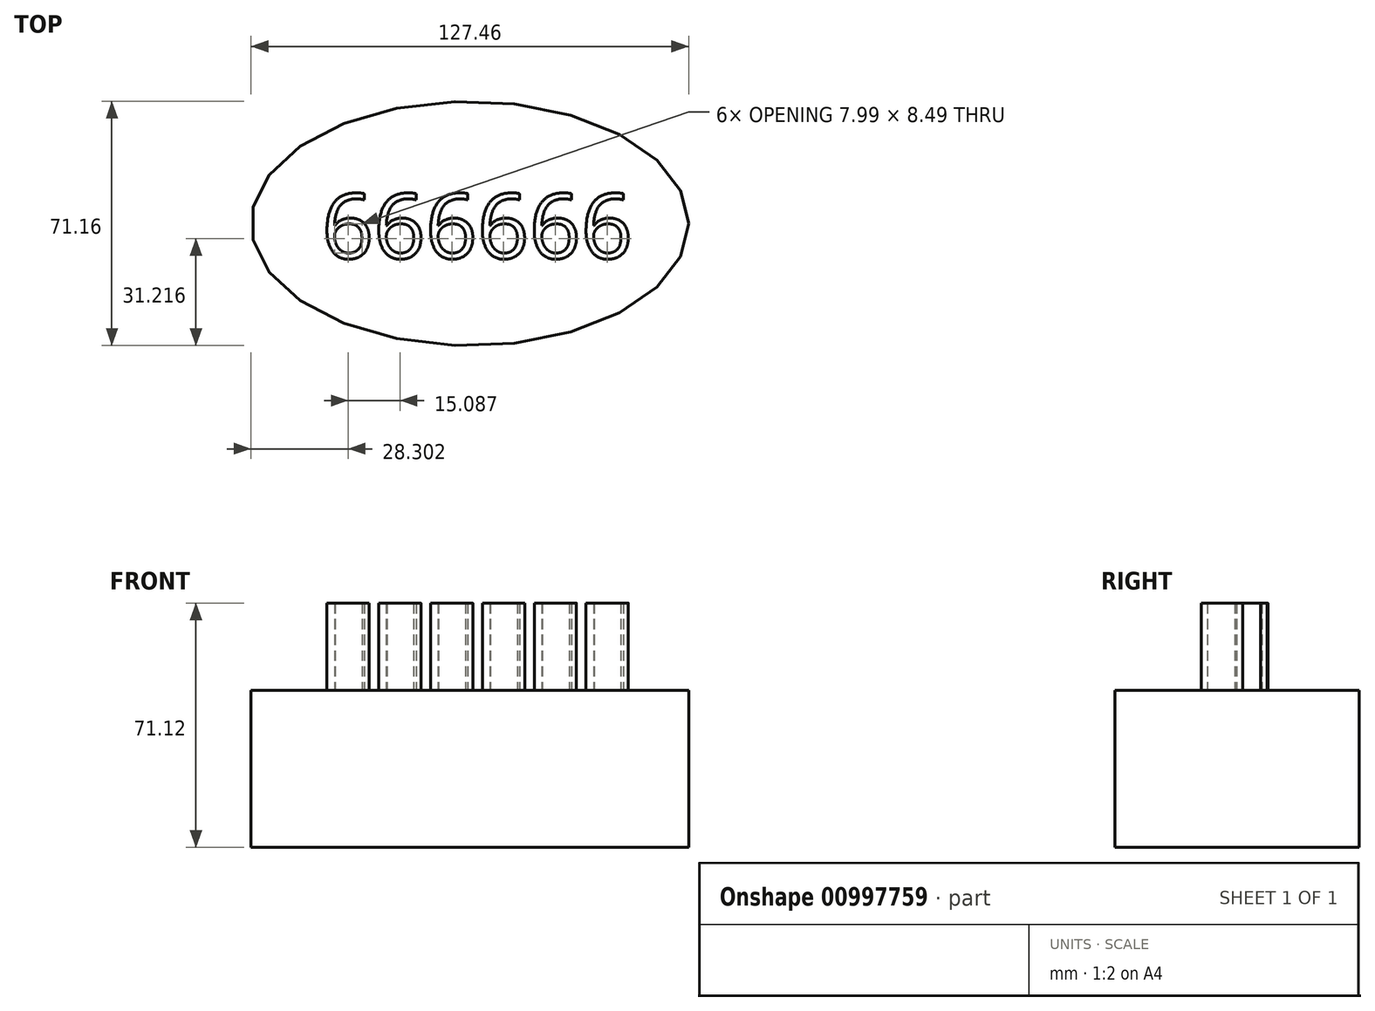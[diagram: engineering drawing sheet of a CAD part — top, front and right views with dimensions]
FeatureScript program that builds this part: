
annotation { "Feature Type Name" : "Feature", "Feature Type Description" : "" }
export const myFeature = defineFeature(function(context is Context, id is Id, definition is map)
    precondition{}
    {
        {
            var Q0;
            Q0=qCreatedBy(makeId("Top.planeOp"),FACE);
            var sketch = newSketch(context, id + "F0", { "sketchPlane" : qUnion([Q0])});
            skEllipse(sketch, "E0", {"center": v(0, 0) * mm, "majorRadius": 63.73 * mm, "minorRadius": 35.58 * mm, "majorAxis": v(1, 0)});
            skSolve(sketch);
        }
        {
            var Q0;
            Q0=makeQuery(id+"F0.imprint","IMPRINT",FACE,{"disambiguationData":[TD([[makeQuery(id+"F0.imprint","IMPRINT",EDGE,{"derivedFrom":sQuery(id+"F0.wireOp",EDGE,"E0")}),1.0]])]});
            extrude(context, id + "F1", {"entities" : qUnion([Q0]), "depth" : 45.72 * mm, "offsetDistance" : 25.4 * mm});
        }
        {
            var Q0;
            Q0=makeQuery(id+"F1.opExtrude","CAP_FACE",FACE,{"disambiguationData":[OSD([sQuery(id+"F0.wireOp",EDGE,"E0")])],"isStart":false});
            var sketch = newSketch(context, id + "F2", { "sketchPlane" : qUnion([Q0])});
            skText(sketch, "E1", { "text": "666666\n", "fontName": "OpenSans-Regular.ttf"});
            const initialGuessF2  = {"E1": [-0.04312, -0.01017, 1, 0, 0.019]};
            skSetInitialGuess(sketch, initialGuessF2);
            skSolve(sketch);
        }
        {
            var Q0;
            Q0 = qSketchRegion(id + "F2", true);
            extrude(context, id + "F3", {"entities" : qUnion([Q0]), "depth" : 25.4 * mm, "offsetDistance" : 25.4 * mm});
        }
    });
